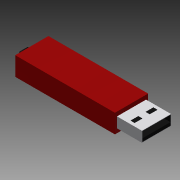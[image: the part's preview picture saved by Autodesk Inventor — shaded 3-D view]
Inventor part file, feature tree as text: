
AUTODESK INVENTOR PART (.ipt)
format: ipt  version: 2015 (Build 190159000, 159)  size: 151,552 bytes
history: native  units: in
note: dims shown in document units (in); Inventor stores cm internally (conversion verified against a paired STEP export)
features: extrude x7, sketch x7
ambient origin geometry x8: Origin, YZ Plane, XZ Plane, XY Plane, X Axis, Y Axis, Z Axis, Center Point
bodies: Solid1 (feature_tree)
feature tree (14):
  extrude  "Legoblokje"  Depth=0.3543in
  extrude  "USB"  Depth=0.0394in
  extrude  "Afwerking USB"  Depth=0.0787in
  extrude  "Afwerking"  Depth=0.4724in TaperAngle=0.0deg
  extrude  "Afwerking bovenkant"  Depth=0.0079in
  extrude  "Achterkant afwerking"  Depth=0.0591in
  extrude  "afwerking gat"  Depth=0.4724in TaperAngle=0.0deg
  sketch  "Sketch1"  dims[d0=1.8898in d1=0.3543in]
  sketch  "Sketch3"  dims[d4=0.6299in d5=0.0in d28=0.0394in]
  sketch  "Sketch4"  dims[d29=0.0787in d30=0.0787in]
  sketch  "Sketch5"  dims[d31=0.0394in d32=0.4724in d33=0.0in]
  sketch  "Sketch6"  dims[d34=0.0079in d35=0.0079in]
  sketch  "Sketch7"  dims[d36=0.0079in d37=0.0591in]
  sketch  "Sketch8"  dims[d38=0.0079in d39=0.4724in d40=0.0in d41=0.0079in d42=0.0004in d43=0.0in d44=0.1969in d45=0.1969in d46=0.0591in d47=0.0591in d48=0.1378in d49=0.0787in d50=0.0787in d51=0.1476in d52=0.1476in d53=0.0039in d54=0.0in d55=0.0394in d56=0.0394in d57=0.0787in d58=0.0787in d59=0.1575in d60=0.0in d61=0.1181in d62=0.1575in d63=0.0in d67=0.1969in]
